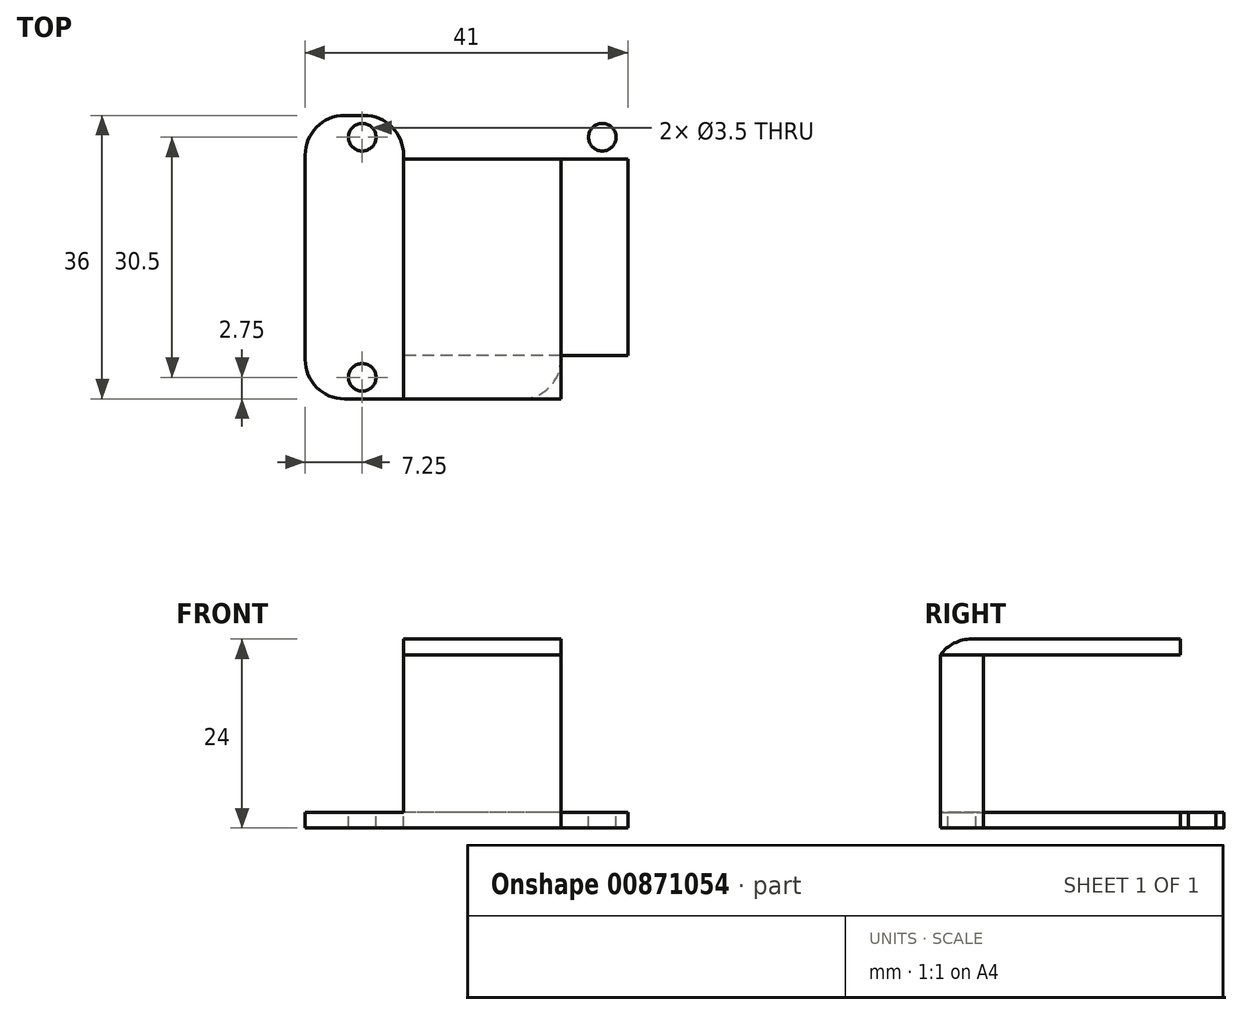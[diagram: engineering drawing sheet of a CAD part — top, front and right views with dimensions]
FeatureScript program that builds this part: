
annotation { "Feature Type Name" : "Feature", "Feature Type Description" : "" }
export const myFeature = defineFeature(function(context is Context, id is Id, definition is map)
    precondition{}
    {
        {
            var Q0;
            Q0=qCreatedBy(makeId("Top.planeOp"),FACE);
            var sketch = newSketch(context, id + "F0", { "sketchPlane" : qUnion([Q0])});
            skLineSegment(sketch, "E0.bottom", {"start": v(15.25, -15.25) * mm, "end": v(-15.25, -15.25) * mm, "construction": true});
            skLineSegment(sketch, "E0.top", {"start": v(15.25, 15.25) * mm, "end": v(-15.25, 15.25) * mm, "construction": true});
            skLineSegment(sketch, "E0.left", {"start": v(15.25, -15.25) * mm, "end": v(15.25, 15.25) * mm, "construction": true});
            skLineSegment(sketch, "E0.right", {"start": v(-15.25, -15.25) * mm, "end": v(-15.25, 15.25) * mm, "construction": true});
            skPoint(sketch, "E0.middle", {"position": v(0, 0) * mm});
            skCircle(sketch, "E1", {"center": v(-15.25, 15.25) * mm, "radius": 1.75 * mm});
            skLineSegment(sketch, "E2", {"start": v(-11.28, 0) * mm, "end": v(10.57, 0) * mm, "construction": true});
            skLineSegment(sketch, "E3", {"start": v(0, 10.05) * mm, "end": v(0, -8.16) * mm, "construction": true});
            skCircle(sketch, "E4.MirrorC", {"center": v(15.25, 15.25) * mm, "radius": 1.75 * mm});
            skCircle(sketch, "E5.MirrorC", {"center": v(-15.25, -15.25) * mm, "radius": 1.75 * mm});
            skCircle(sketch, "E6.MirrorC", {"center": v(15.25, -15.25) * mm, "radius": 1.75 * mm});
            skLineSegment(sketch, "E7.bottom", {"start": v(22.5, -18) * mm, "end": v(-22.5, -18) * mm});
            skLineSegment(sketch, "E7.top", {"start": v(22.5, 18) * mm, "end": v(-22.5, 18) * mm});
            skLineSegment(sketch, "E7.left", {"start": v(22.5, -18) * mm, "end": v(22.5, 18) * mm});
            skLineSegment(sketch, "E7.right", {"start": v(-22.5, -18) * mm, "end": v(-22.5, 18) * mm});
            skLineSegment(sketch, "E8.bottom", {"start": v(18.5, -12.5) * mm, "end": v(-18.5, -12.5) * mm});
            skLineSegment(sketch, "E8.top", {"start": v(18.5, 12.5) * mm, "end": v(-18.5, 12.5) * mm});
            skLineSegment(sketch, "E8.left", {"start": v(18.5, -12.5) * mm, "end": v(18.5, 12.5) * mm});
            skLineSegment(sketch, "E8.right", {"start": v(-18.5, -12.5) * mm, "end": v(-18.5, 12.5) * mm});
            skLineSegment(sketch, "E9.right", {"start": v(-19.5, -13.5) * mm, "end": v(-19.5, 13.5) * mm});
            skLineSegment(sketch, "E10", {"start": v(0, 18) * mm, "end": v(-10, 18) * mm});
            skLineSegment(sketch, "E11", {"start": v(-10, 18) * mm, "end": v(-10, 12.5) * mm});
            skLineSegment(sketch, "E12.MirrorCS", {"start": v(10, 18) * mm, "end": v(10, 12.5) * mm});
            skLineSegment(sketch, "E13.MirrorCS", {"start": v(-10, -18) * mm, "end": v(-10, -12.5) * mm});
            skLineSegment(sketch, "E14.MirrorCS", {"start": v(10, -18) * mm, "end": v(10, -12.5) * mm});
            skLineSegment(sketch, "E15", {"start": v(-10, 12.5) * mm, "end": v(-10, -12.5) * mm});
            skLineSegment(sketch, "E16", {"start": v(10, 12.5) * mm, "end": v(10, -12.5) * mm});
            skSolve(sketch);
        }
        {
            var Q0;
            {var subQ0=sQuery(id+"F0.wireOp",EDGE,"E8.right");Q0=makeQuery(id+"F0.imprint","IMPRINT",FACE,{"disambiguationData":[TD([[makeQuery(id+"F0.imprint","IMPRINT",EDGE,{"derivedFrom":subQ0}),-1.0]])]});}
            var Q1;
            Q1=makeQuery(id+"F0.imprint","IMPRINT",FACE,{"disambiguationData":[TD([[makeQuery(id+"F0.imprint","IMPRINT",EDGE,{"derivedFrom":sQuery(id+"F0.wireOp",EDGE,"E1")}),-1.0]])]});
            var Q2;
            Q2=makeQuery(id+"F0.imprint","IMPRINT",FACE,{"disambiguationData":[TD([[makeQuery(id+"F0.imprint","IMPRINT",EDGE,{"derivedFrom":sQuery(id+"F0.wireOp",EDGE,"E4.MirrorC")}),1.0]])]});
            var Q3;
            {var subQ0=sQuery(id+"F0.wireOp",EDGE,"E8.left");Q3=makeQuery(id+"F0.imprint","IMPRINT",FACE,{"disambiguationData":[TD([[makeQuery(id+"F0.imprint","IMPRINT",EDGE,{"derivedFrom":subQ0}),1.0]])]});}
            var Q4;
            {var subQ0=sQuery(id+"F0.wireOp",EDGE,"E15");Q4=makeQuery(id+"F0.imprint","IMPRINT",FACE,{"disambiguationData":[TD([[makeQuery(id+"F0.imprint","IMPRINT",EDGE,{"derivedFrom":subQ0}),1.0]])]});}
            var Q5;
            {var subQ0=sQuery(id+"F0.wireOp",EDGE,"E10");Q5=makeQuery(id+"F0.imprint","IMPRINT",FACE,{"disambiguationData":[TD([[makeQuery(id+"F0.imprint","IMPRINT",EDGE,{"derivedFrom":subQ0}),1.0]])]});}
            var Q6;
            {var subQ0=sQuery(id+"F0.wireOp",EDGE,"E13.MirrorCS");Q6=makeQuery(id+"F0.imprint","IMPRINT",FACE,{"disambiguationData":[TD([[makeQuery(id+"F0.imprint","IMPRINT",EDGE,{"derivedFrom":subQ0}),-1.0]])]});}
            extrude(context, id + "F1", {"entities" : qUnion([Q0, Q1, Q2, Q3, Q4, Q5, Q6]), "oppositeDirection" : true, "depth" : 2 * mm, "offsetDistance" : 25 * mm});
        }
        {
            var Q0;
            {var subQ0=sQuery(id+"F0.wireOp",EDGE,"E10");Q0=makeQuery(id+"F0.imprint","IMPRINT",FACE,{"disambiguationData":[TD([[makeQuery(id+"F0.imprint","IMPRINT",EDGE,{"derivedFrom":subQ0}),1.0]])]});}
            var Q1;
            {var subQ0=sQuery(id+"F0.wireOp",EDGE,"E13.MirrorCS");Q1=makeQuery(id+"F0.imprint","IMPRINT",FACE,{"disambiguationData":[TD([[makeQuery(id+"F0.imprint","IMPRINT",EDGE,{"derivedFrom":subQ0}),-1.0]])]});}
            extrude(context, id + "F2", {"entities" : qUnion([Q0, Q1]), "operationType" : NewBodyOperationType.ADD, "depth" : 20 * mm, "offsetDistance" : 25 * mm});
        }
        {
            var Q0;
            {var subQ0=sQuery(id+"F0.wireOp",EDGE,"E10");Q0=makeQuery(id+"F0.imprint","IMPRINT",FACE,{"disambiguationData":[TD([[makeQuery(id+"F0.imprint","IMPRINT",EDGE,{"derivedFrom":subQ0}),1.0]])]});}
            var Q1;
            {var subQ0=sQuery(id+"F0.wireOp",EDGE,"E15");Q1=makeQuery(id+"F0.imprint","IMPRINT",FACE,{"disambiguationData":[TD([[makeQuery(id+"F0.imprint","IMPRINT",EDGE,{"derivedFrom":subQ0}),1.0]])]});}
            var Q2;
            {var subQ0=sQuery(id+"F0.wireOp",EDGE,"E13.MirrorCS");Q2=makeQuery(id+"F0.imprint","IMPRINT",FACE,{"disambiguationData":[TD([[makeQuery(id+"F0.imprint","IMPRINT",EDGE,{"derivedFrom":subQ0}),-1.0]])]});}
            extrude(context, id + "F3", {"entities" : qUnion([Q0, Q1, Q2]), "depth" : 2 * mm, "offsetDistance" : 25 * mm});
        }
        {
            var Q0;
            Q0=makeQuery(id+"F3.opExtrude","SWEPT_BODY",BODY,{"disambiguationData":[OSD([sQuery(id+"F0.wireOp",EDGE,"E7.bottom"),sQuery(id+"F0.wireOp",EDGE,"E7.top"),sQuery(id+"F0.wireOp",EDGE,"E10"),sQuery(id+"F0.wireOp",EDGE,"E11"),sQuery(id+"F0.wireOp",EDGE,"E12.MirrorCS"),sQuery(id+"F0.wireOp",EDGE,"E13.MirrorCS"),sQuery(id+"F0.wireOp",EDGE,"E14.MirrorCS"),sQuery(id+"F0.wireOp",EDGE,"E15"),sQuery(id+"F0.wireOp",EDGE,"E16")])]});
            var Q1;
            Q1=makeQuery(id+"F2.opExtrude","SWEPT_EDGE",EDGE,{"disambiguationData":[OSD([sQuery(id+"F0.wireOp",EDGE,"E7.bottom"),sQuery(id+"F0.wireOp",EDGE,"E13.MirrorCS")])]});
            transform(context, id + "F4", {"entities" : qUnion([Q0]), "transformType" : TransformType.TRANSLATION_DISTANCE, "transformDirection" : qUnion([Q1]), "distance" : 20 * mm, "oppositeDirection" : true, "makeCopy" : false});
        }
        {
            var Q0;
            Q0=makeQuery(id+"F2.opExtrude","CAP_EDGE",EDGE,{"disambiguationData":[OSD([sQuery(id+"F0.wireOp",EDGE,"E11")])],"isStart":true});
            var Q1;
            Q1=makeQuery(id+"F2.opExtrude","CAP_EDGE",EDGE,{"disambiguationData":[OSD([sQuery(id+"F0.wireOp",EDGE,"E13.MirrorCS")])],"isStart":true});
            var Q2;
            Q2=makeQuery(id+"F2.opExtrude","CAP_EDGE",EDGE,{"disambiguationData":[OSD([sQuery(id+"F0.wireOp",EDGE,"E12.MirrorCS")])],"isStart":true});
            var Q3;
            Q3=makeQuery(id+"F2.opExtrude","CAP_EDGE",EDGE,{"disambiguationData":[OSD([sQuery(id+"F0.wireOp",EDGE,"E14.MirrorCS")])],"isStart":true});
            var Q4;
            Q4=makeQuery(id+"F3.opExtrude","CAP_EDGE",EDGE,{"disambiguationData":[OSD([sQuery(id+"F0.wireOp",EDGE,"E7.bottom")])],"isStart":false});
            var Q5;
            Q5=makeQuery(id+"F3.opExtrude","CAP_EDGE",EDGE,{"disambiguationData":[OSD([sQuery(id+"F0.wireOp",EDGE,"E7.top"),sQuery(id+"F0.wireOp",EDGE,"E10")])],"isStart":false});
            var Q6;
            Q6=makeQuery(id+"F1.opExtrude","SWEPT_EDGE",EDGE,{"disambiguationData":[OSD([sQuery(id+"F0.wireOp",EDGE,"E7.bottom"),sQuery(id+"F0.wireOp",EDGE,"E7.left")])]});
            var Q7;
            Q7=makeQuery(id+"F1.opExtrude","SWEPT_EDGE",EDGE,{"disambiguationData":[OSD([sQuery(id+"F0.wireOp",EDGE,"E7.top"),sQuery(id+"F0.wireOp",EDGE,"E7.left")])]});
            var Q8;
            Q8=makeQuery(id+"F1.opExtrude","SWEPT_EDGE",EDGE,{"disambiguationData":[OSD([sQuery(id+"F0.wireOp",EDGE,"E7.top"),sQuery(id+"F0.wireOp",EDGE,"E7.right")])]});
            var Q9;
            Q9=makeQuery(id+"F1.opExtrude","SWEPT_EDGE",EDGE,{"disambiguationData":[OSD([sQuery(id+"F0.wireOp",EDGE,"E7.bottom"),sQuery(id+"F0.wireOp",EDGE,"E7.right")])]});
            fillet(context, id + "F5", {"entities" : qUnion([Q0, Q1, Q2, Q3, Q4, Q5, Q6, Q7, Q8, Q9]), "radius" : 5 * mm, "tangentPropagation" : true, "allowEdgeOverflow" : false});
        }
    });
